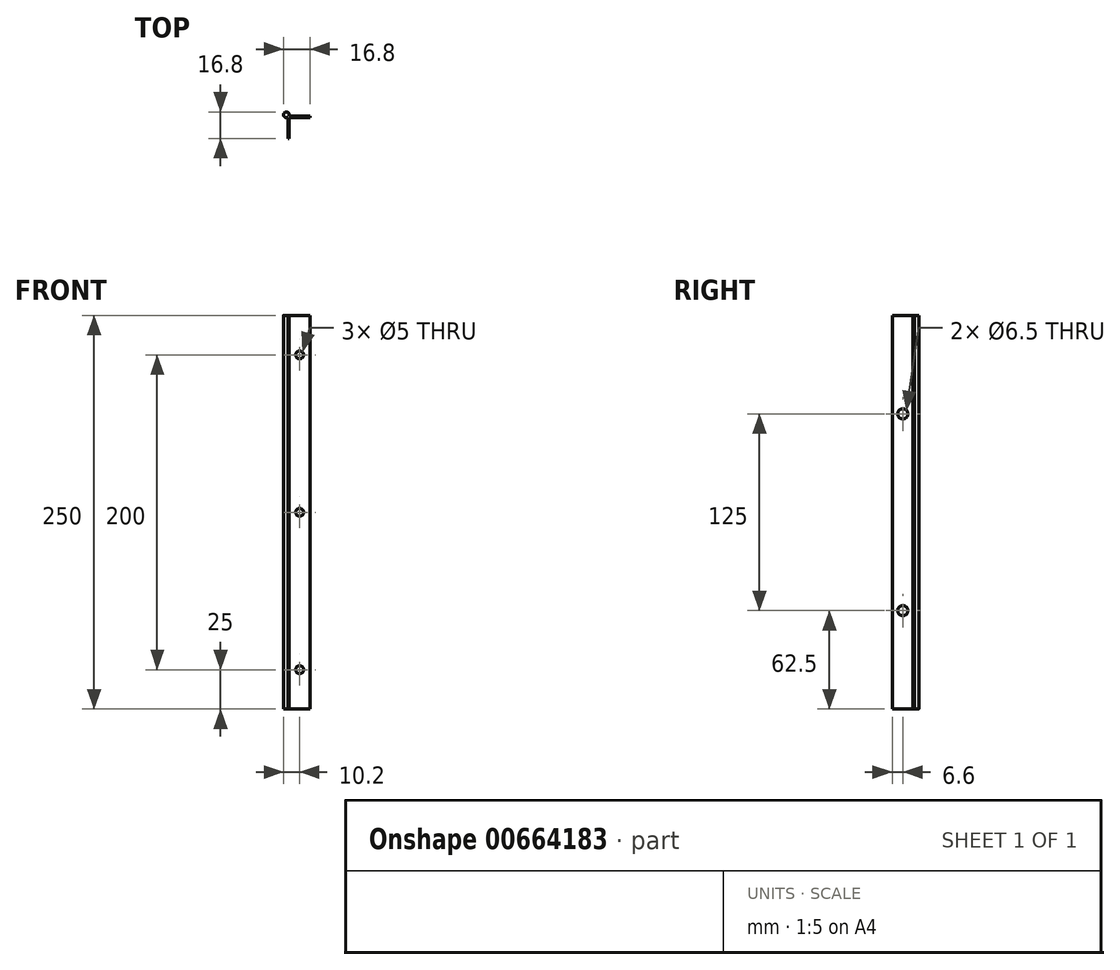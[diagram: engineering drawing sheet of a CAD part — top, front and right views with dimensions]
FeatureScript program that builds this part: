
annotation { "Feature Type Name" : "Feature", "Feature Type Description" : "" }
export const myFeature = defineFeature(function(context is Context, id is Id, definition is map)
    precondition{}
    {
        {
            var Q0;
            Q0=qCreatedBy(makeId("Top.planeOp"),FACE);
            var sketch = newSketch(context, id + "F0", { "sketchPlane" : qUnion([Q0])});
            skLineSegment(sketch, "E0", {"start": v(0, 0) * mm, "end": v(0, -13.2) * mm});
            skLineSegment(sketch, "E1", {"start": v(0, -13.2) * mm, "end": v(-0.8, -13.2) * mm});
            skLineSegment(sketch, "E2", {"start": v(-0.8, -13.2) * mm, "end": v(-0.8, 0) * mm});
            skLineSegment(sketch, "E3", {"start": v(0, 0.8) * mm, "end": v(13.2, 0.8) * mm});
            skLineSegment(sketch, "E4", {"start": v(13.2, 0.8) * mm, "end": v(13.2, 0) * mm});
            skLineSegment(sketch, "E5", {"start": v(13.2, 0) * mm, "end": v(0, 0) * mm});
            skCircle(sketch, "E6", {"center": v(-1.8, 1.8) * mm, "radius": 1.8 * mm});
            skLineSegment(sketch, "E7", {"start": v(-0.8, 0) * mm, "end": v(-1.8, 0) * mm});
            skLineSegment(sketch, "E8", {"start": v(0, 0.8) * mm, "end": v(0, 1.8) * mm});
            skSolve(sketch);
        }
        {
            var Q0;
            {var subQ0=sQuery(id+"F0.wireOp",EDGE,"E6");var subQ1=makeQuery(id+"F0.imprint","INTERSECT",VERTEX,{"derivedFrom":[subQ0,sQuery(id+"F0.wireOp",EDGE,"E7")]});Q0=makeQuery(id+"F0.imprint","IMPRINT",FACE,{"disambiguationData":[TD([[makeQuery(id+"F0.imprint","IMPRINT",EDGE,{"disambiguationData":[TD([[subQ1,1.0]])],"derivedFrom":subQ0}),1.0]])]});}
            var Q1;
            Q1=makeQuery(id+"F0.imprint","IMPRINT",FACE,{"disambiguationData":[TD([[makeQuery(id+"F0.imprint","IMPRINT",EDGE,{"derivedFrom":sQuery(id+"F0.wireOp",EDGE,"E0")}),-1.0]])]});
            extrude(context, id + "F1", {"entities" : qUnion([Q0, Q1]), "depth" : 250 * mm});
        }
        {
            var Q0;
            Q0=makeQuery(id+"F1.opExtrude","SWEPT_FACE",FACE,{"disambiguationData":[OSD([sQuery(id+"F0.wireOp",EDGE,"E3")])]});
            var sketch = newSketch(context, id + "F2", { "sketchPlane" : qUnion([Q0])});
            skCircle(sketch, "E9", {"center": v(-6.6, 225) * mm, "radius": 2.5 * mm});
            skCircle(sketch, "E10", {"center": v(-6.6, 125) * mm, "radius": 2.5 * mm});
            skCircle(sketch, "E11", {"center": v(-6.6, 25) * mm, "radius": 2.5 * mm});
            skLineSegment(sketch, "E12", {"start": v(-6.6, 250) * mm, "end": v(-6.6, 0) * mm, "construction": true});
            skSolve(sketch);
        }
        {
            var Q0;
            Q0=makeQuery(id+"F2.imprint","IMPRINT",FACE,{"disambiguationData":[TD([[makeQuery(id+"F2.imprint","IMPRINT",EDGE,{"derivedFrom":sQuery(id+"F2.wireOp",EDGE,"E11")}),1.0]])]});
            var Q1;
            Q1=makeQuery(id+"F2.imprint","IMPRINT",FACE,{"disambiguationData":[TD([[makeQuery(id+"F2.imprint","IMPRINT",EDGE,{"derivedFrom":sQuery(id+"F2.wireOp",EDGE,"E10")}),1.0]])]});
            var Q2;
            Q2=makeQuery(id+"F2.imprint","IMPRINT",FACE,{"disambiguationData":[TD([[makeQuery(id+"F2.imprint","IMPRINT",EDGE,{"derivedFrom":sQuery(id+"F2.wireOp",EDGE,"E9")}),1.0]])]});
            extrude(context, id + "F3", {"entities" : qUnion([Q0, Q1, Q2]), "operationType" : NewBodyOperationType.REMOVE, "endBound" : BoundingType.THROUGH_ALL, "oppositeDirection" : true, "depth" : 25 * mm, "offsetDistance" : 25 * mm});
        }
        {
            var Q0;
            Q0=makeQuery(id+"F1.opExtrude","SWEPT_FACE",FACE,{"disambiguationData":[OSD([sQuery(id+"F0.wireOp",EDGE,"E0")])]});
            var sketch = newSketch(context, id + "F4", { "sketchPlane" : qUnion([Q0])});
            skLineSegment(sketch, "E13", {"start": v(-6.6, 250) * mm, "end": v(-6.6, 0) * mm, "construction": true});
            skCircle(sketch, "E14", {"center": v(-6.6, 62.5) * mm, "radius": 3.25 * mm});
            skCircle(sketch, "E15", {"center": v(-6.6, 125) * mm, "radius": 3.25 * mm});
            skCircle(sketch, "E16", {"center": v(-6.6, 187.5) * mm, "radius": 3.25 * mm});
            skSolve(sketch);
        }
        {
            var Q0;
            Q0=makeQuery(id+"F4.imprint","IMPRINT",FACE,{"disambiguationData":[TD([[makeQuery(id+"F4.imprint","IMPRINT",EDGE,{"derivedFrom":sQuery(id+"F4.wireOp",EDGE,"E16")}),1.0]])]});
            var Q1;
            Q1=makeQuery(id+"F4.imprint","IMPRINT",FACE,{"disambiguationData":[TD([[makeQuery(id+"F4.imprint","IMPRINT",EDGE,{"derivedFrom":sQuery(id+"F4.wireOp",EDGE,"E14")}),1.0]])]});
            extrude(context, id + "F5", {"entities" : qUnion([Q0, Q1]), "operationType" : NewBodyOperationType.REMOVE, "endBound" : BoundingType.THROUGH_ALL, "oppositeDirection" : true, "depth" : 25 * mm, "offsetDistance" : 25 * mm});
        }
    });
